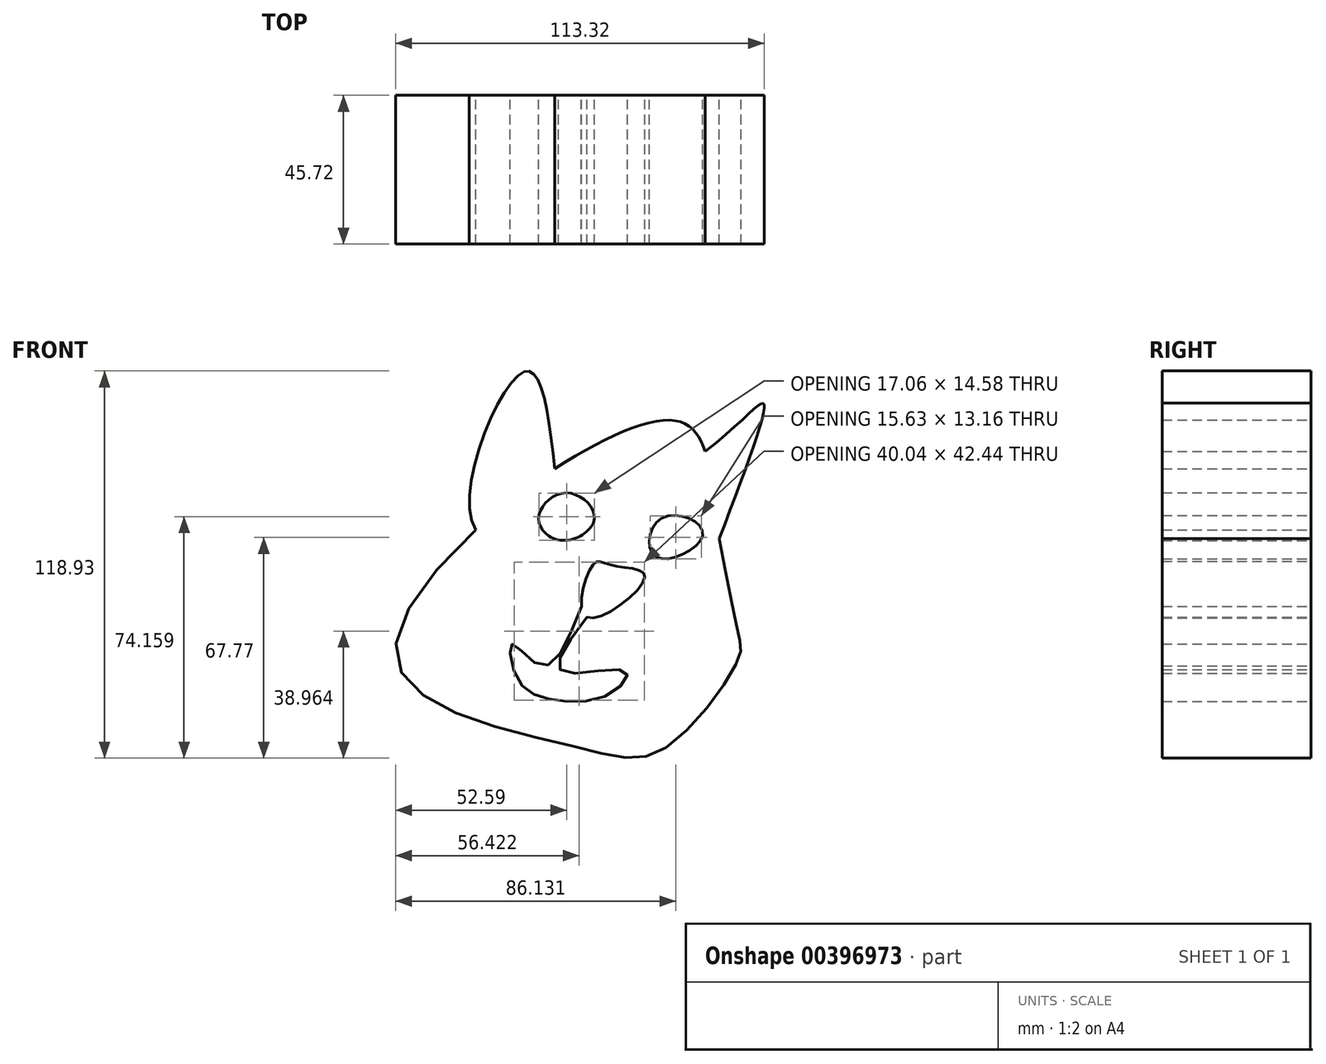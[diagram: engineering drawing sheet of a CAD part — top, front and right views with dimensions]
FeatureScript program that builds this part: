
annotation { "Feature Type Name" : "Feature", "Feature Type Description" : "" }
export const myFeature = defineFeature(function(context is Context, id is Id, definition is map)
    precondition{}
    {
        {
            var Q0;
            Q0=qCreatedBy(makeId("Front.planeOp"),FACE);
            var sketch = newSketch(context, id + "F0", { "sketchPlane" : qUnion([Q0])});
            skFitSpline(sketch, "E0", {"points": [v(32.8, 34.89) * mm, v(-51.2, -35.64) * mm, v(2.84, -65.22) * mm, v(31.28, -66.17) * mm, v(54.04, -38.87) * mm, v(54.41, -31.85) * mm, v(46.83, 8.15) * mm, v(32.8, 34.89) * mm]});
            skFitSpline(sketch, "E1", {"points": [v(-2.23, 19.91) * mm, v(-11.94, 49.67) * mm, v(-26.53, 1.1) * mm, v(43.91, 25.25) * mm, v(62, 39.82) * mm, v(48.31, -1.53) * mm], "startDerivative": vector(-32.79, 285.55) * mm, "endDerivative": vector(-110.22, -290) * mm});
            skFitSpline(sketch, "E2", {"points": [v(9.67, -9.3) * mm, v(14.98, -9.67) * mm, v(25.4, -13.27) * mm, v(7.58, -25.6) * mm, v(9.67, -9.3) * mm]});
            skFitSpline(sketch, "E3", {"points": [v(30.53, 4.74) * mm, v(43.23, 0) * mm, v(29, -7.2) * mm, v(30.53, 4.74) * mm]});
            skFitSpline(sketch, "E4", {"points": [v(1.33, 12.51) * mm, v(9.93, 4.74) * mm, v(0, -2.09) * mm, v(-7.2, 4.74) * mm, v(1.33, 12.51) * mm]});
            skFitSpline(sketch, "E5", {"points": [v(7.58, -25.6) * mm, v(0, -42.28) * mm, v(19.53, -42.28) * mm, v(14.6, -49.3) * mm, v(-3.8, -50.81) * mm, v(-13.65, -44.74) * mm, v(-15.36, -33.94) * mm, v(-6.45, -40.57) * mm, v(5.95, -22.3) * mm], "startDerivative": vector(-119.18, -158.6) * mm, "endDerivative": vector(73.71, 189.25) * mm});
            skSolve(sketch);
        }
        {
            var Q0;
            {var subQ0=sQuery(id+"F0.wireOp",EDGE,"E1");var subQ1=sQuery(id+"F0.wireOp",EDGE,"E0");var subQ2=makeQuery(id+"F0.imprint","INTERSECT",VERTEX,{"disambiguationData":[OD(0.0)],"derivedFrom":[subQ1,subQ0]});Q0=makeQuery(id+"F0.imprint","IMPRINT",FACE,{"disambiguationData":[TD([[makeQuery(id+"F0.imprint","IMPRINT",EDGE,{"disambiguationData":[TD([[subQ2,-1.0]])],"derivedFrom":subQ1}),-1.0]])]});}
            var Q1;
            {var subQ0=sQuery(id+"F0.wireOp",EDGE,"E1");var subQ1=sQuery(id+"F0.wireOp",EDGE,"E0");var subQ2=makeQuery(id+"F0.imprint","INTERSECT",VERTEX,{"disambiguationData":[OD(1.0)],"derivedFrom":[subQ1,subQ0]});Q1=makeQuery(id+"F0.imprint","IMPRINT",FACE,{"disambiguationData":[TD([[makeQuery(id+"F0.imprint","IMPRINT",EDGE,{"disambiguationData":[TD([[subQ2,-1.0]])],"derivedFrom":subQ1}),-1.0]])]});}
            var Q2;
            {var subQ0=sQuery(id+"F0.wireOp",EDGE,"E1");var subQ1=sQuery(id+"F0.wireOp",EDGE,"E0");var subQ5=makeQuery(id+"F0.imprint","INTERSECT",VERTEX,{"disambiguationData":[OD(0.0)],"derivedFrom":[subQ1,subQ0]});Q2=makeQuery(id+"F0.imprint","IMPRINT",FACE,{"disambiguationData":[TD([[makeQuery(id+"F0.imprint","IMPRINT",EDGE,{"disambiguationData":[TD([[subQ5,-1.0]])],"derivedFrom":subQ1}),1.0]])]});}
            var Q3;
            Q3=makeQuery(id+"F0.imprint","IMPRINT",FACE,{"disambiguationData":[TD([[makeQuery(id+"F0.imprint","IMPRINT",EDGE,{"derivedFrom":sQuery(id+"F0.wireOp",EDGE,"E3")}),1.0]])]});
            extrude(context, id + "F1", {"entities" : qUnion([Q0, Q1, Q2, Q3]), "depth" : 45.72 * mm});
        }
    });
